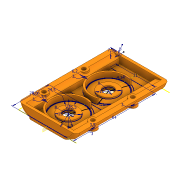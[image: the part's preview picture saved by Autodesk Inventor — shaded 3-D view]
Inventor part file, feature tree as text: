
AUTODESK INVENTOR PART (.ipt)
format: ipt  version: 2020.3 (Build 243373000, 373)  size: 320,000 bytes
history: native  units: mm
features: extrude x11, sketch x4, plane x1, mirror x1, fillet x1
ambient origin geometry x8: Origin, YZ Plane, XZ Plane, XY Plane, X Axis, Y Axis, Z Axis, Center Point
bodies: Solid1 (feature_tree)
feature tree (18):
  extrude  "Extrusion1"  Depth=72.2mm
  sketch  "Sketch2"  dims[d2=2.0mm d3=0.0mm d4=31.0mm]
  extrude  "Extrusion2"  Depth=31.0mm
  extrude  "Extrusion3"  Depth=24.5mm
  extrude  "Extrusion4"  Depth=2.75mm
  sketch  "Sketch4"  dims[d5=64.0mm d6=24.5mm]
  extrude  "Extrusion5"  Depth=2.75mm
  extrude  "Extrusion6"  Depth=2.75mm
  extrude  "Extrusion7"  Depth=2.75mm
  extrude  "Extrusion8"  Depth=2.75mm
  extrude  "Extrusion9"  Depth=2.75mm TaperAngle=0.0deg
  plane  "Work Plane1"
  mirror  "Mirror1"
  extrude  "Extrusion10"  Depth=2.75mm TaperAngle=0.0deg
  fillet  "Fillet1"  Radius=15.0mm
  extrude  "Extrusion11"  Depth=2.75mm
  sketch  "Sketch1"  dims[d0=45.0mm d1=72.2mm]
  sketch  "Sketch6"  dims[d7=28.66mm d8=4.34mm d9=25.5mm d10=28.0mm d12=15.0mm d13=8.0mm d14=4.0mm d15=0.0mm d16=1.0mm d17=0.0mm d18=15.0mm d19=8.0mm d21=1.0mm d22=0.0mm d24=3.0mm d25=3.0mm d26=3.0mm d27=3.0mm d28=3.5mm d29=3.5mm d30=10.0mm d31=7.5mm d32=4.0mm d33=74.75mm d34=0.0mm d35=10.0mm d36=0.0mm d37=8.0mm d38=16.5mm d39=0.0mm d40=6.2mm d41=6.2mm d42=6.0mm d43=0.0mm d44=10.0mm d45=0.0mm d46=-22.5mm d49=2.0mm d50=2.0mm d51=5.75mm d52=0.0mm d53=2.75mm d54=8.0mm d55=0.0mm]
